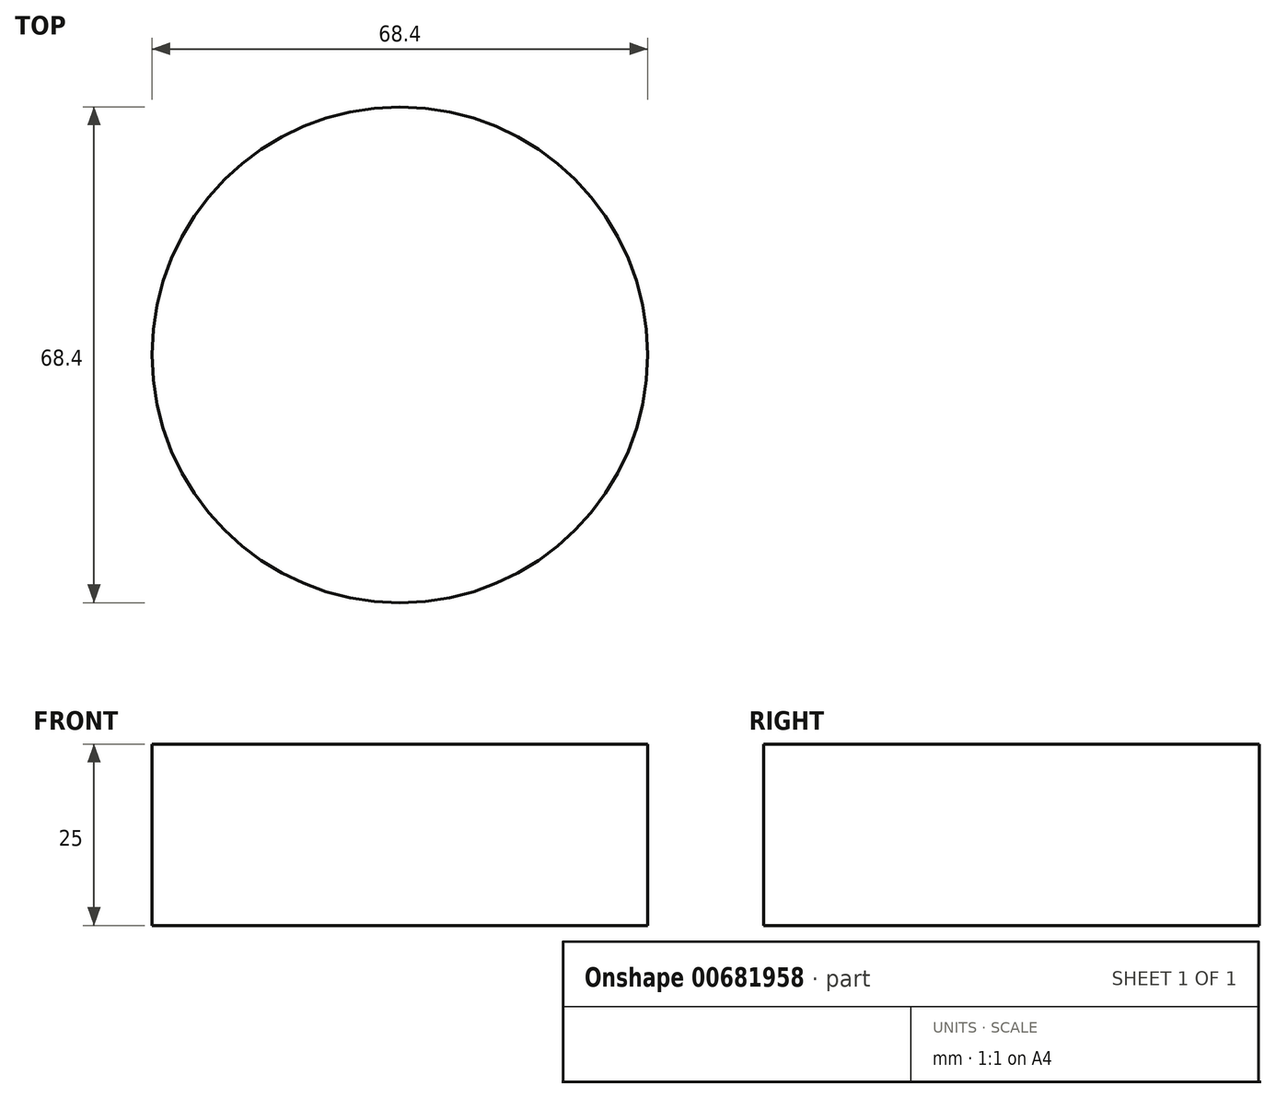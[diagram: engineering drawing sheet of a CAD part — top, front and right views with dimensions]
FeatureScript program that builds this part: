
annotation { "Feature Type Name" : "Feature", "Feature Type Description" : "" }
export const myFeature = defineFeature(function(context is Context, id is Id, definition is map)
    precondition{}
    {
        {
            var Q0;
            Q0=qCreatedBy(makeId("Top.planeOp"),FACE);
            var sketch = newSketch(context, id + "F0", { "sketchPlane" : qUnion([Q0])});
            skCircle(sketch, "E0", {"center": v(0, 0) * mm, "radius": 34.2 * mm});
            skSolve(sketch);
        }
        {
            var Q0;
            Q0 = qSketchRegion(id + "F0", true);
            extrude(context, id + "F1", {"entities" : qUnion([Q0]), "depth" : 25 * mm, "offsetDistance" : 25 * mm});
        }
    });
